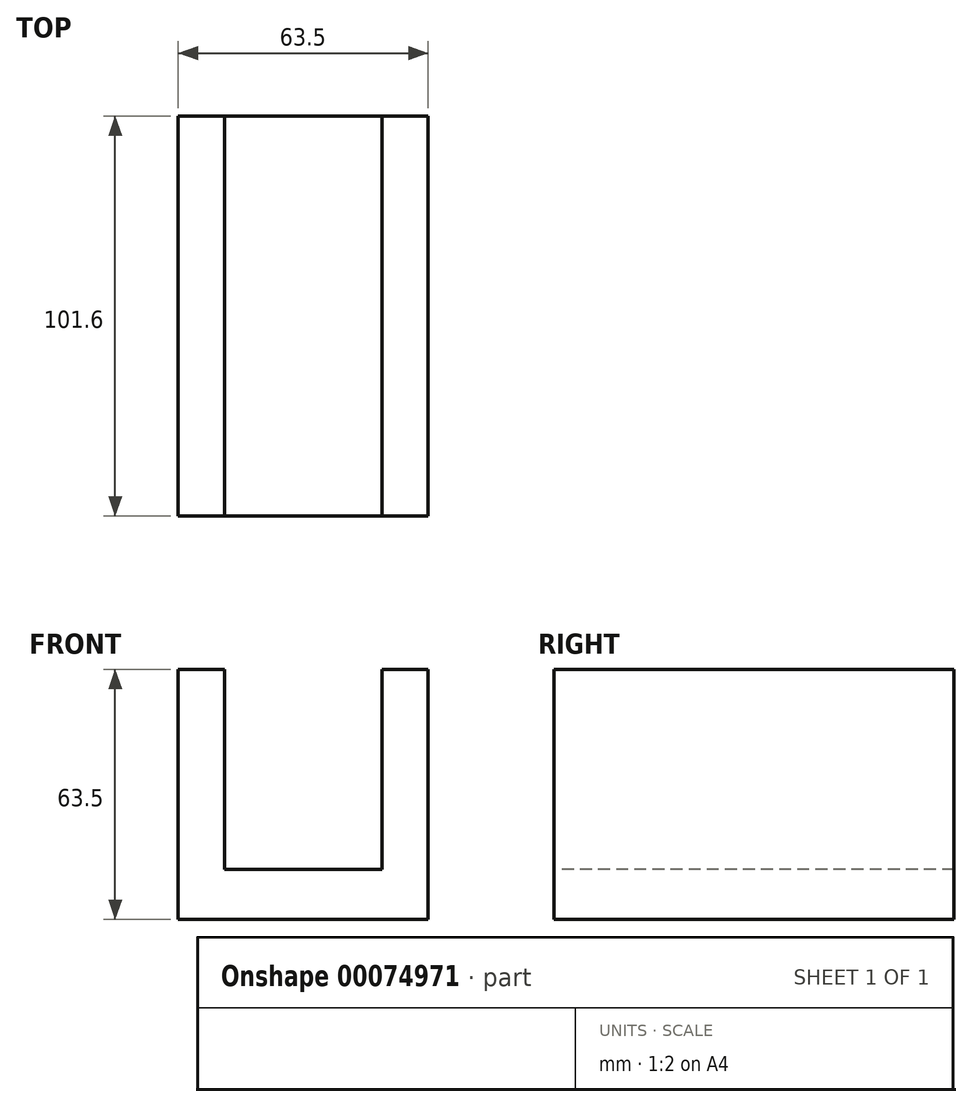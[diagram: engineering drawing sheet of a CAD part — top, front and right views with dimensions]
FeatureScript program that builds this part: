
annotation { "Feature Type Name" : "Feature", "Feature Type Description" : "" }
export const myFeature = defineFeature(function(context is Context, id is Id, definition is map)
    precondition{}
    {
        {
            var Q0;
            Q0=qCreatedBy(makeId("Top.planeOp"),FACE);
            var sketch = newSketch(context, id + "F0", { "sketchPlane" : qUnion([Q0])});
            skLineSegment(sketch, "E0", {"start": v(-31.75, 0) * mm, "end": v(-31.75, 50.8) * mm});
            skLineSegment(sketch, "E1", {"start": v(-31.75, 50.8) * mm, "end": v(0, 50.8) * mm});
            skLineSegment(sketch, "E2.MirrorCS", {"start": v(-31.75, 0) * mm, "end": v(-31.75, -50.8) * mm});
            skLineSegment(sketch, "E3.MirrorCS", {"start": v(-31.75, -50.8) * mm, "end": v(0, -50.8) * mm});
            skLineSegment(sketch, "E4.MirrorCS", {"start": v(31.75, 50.8) * mm, "end": v(0, 50.8) * mm});
            skLineSegment(sketch, "E5.MirrorCS", {"start": v(31.75, 0) * mm, "end": v(31.75, 50.8) * mm});
            skLineSegment(sketch, "E6.MirrorCS", {"start": v(31.75, 0) * mm, "end": v(31.75, -50.8) * mm});
            skLineSegment(sketch, "E7.MirrorCS", {"start": v(31.75, -50.8) * mm, "end": v(0, -50.8) * mm});
            skSolve(sketch);
        }
        {
            var Q0;
            Q0=makeQuery(id+"F0.imprint","IMPRINT",FACE,{"disambiguationData":[TD([[makeQuery(id+"F0.imprint","IMPRINT",EDGE,{"derivedFrom":sQuery(id+"F0.wireOp",EDGE,"E0")}),-1.0]])]});
            extrude(context, id + "F1", {"entities" : qUnion([Q0]), "depth" : 12.7 * mm});
        }
        {
            var Q0;
            Q0=makeQuery(id+"F1.opExtrude","CAP_FACE",FACE,{"disambiguationData":[OSD([sQuery(id+"F0.wireOp",EDGE,"E0"),sQuery(id+"F0.wireOp",EDGE,"E1"),sQuery(id+"F0.wireOp",EDGE,"E2.MirrorCS"),sQuery(id+"F0.wireOp",EDGE,"E3.MirrorCS"),sQuery(id+"F0.wireOp",EDGE,"E4.MirrorCS"),sQuery(id+"F0.wireOp",EDGE,"E5.MirrorCS"),sQuery(id+"F0.wireOp",EDGE,"E6.MirrorCS"),sQuery(id+"F0.wireOp",EDGE,"E7.MirrorCS")])],"isStart":false});
            var sketch = newSketch(context, id + "F2", { "sketchPlane" : qUnion([Q0])});
            skLineSegment(sketch, "E8", {"start": v(20.03, 50.8) * mm, "end": v(20.03, -50.8) * mm});
            skLineSegment(sketch, "E9.MirrorCS", {"start": v(-20.03, 50.8) * mm, "end": v(-20.03, -50.8) * mm});
            skSolve(sketch);
        }
        {
            var Q0;
            {var subQ0=sQuery(id+"F2.wireOp",EDGE,"E9.MirrorCS");Q0=makeQuery(id+"F2.imprint","IMPRINT",FACE,{"disambiguationData":[TD([[makeQuery(id+"F2.imprint","IMPRINT",EDGE,{"derivedFrom":subQ0}),-1.0]])]});}
            var Q1;
            {var subQ0=sQuery(id+"F2.wireOp",EDGE,"E8");Q1=makeQuery(id+"F2.imprint","IMPRINT",FACE,{"disambiguationData":[TD([[makeQuery(id+"F2.imprint","IMPRINT",EDGE,{"derivedFrom":subQ0}),1.0]])]});}
            extrude(context, id + "F3", {"entities" : qUnion([Q0, Q1]), "operationType" : NewBodyOperationType.ADD, "depth" : 50.8 * mm});
        }
    });
